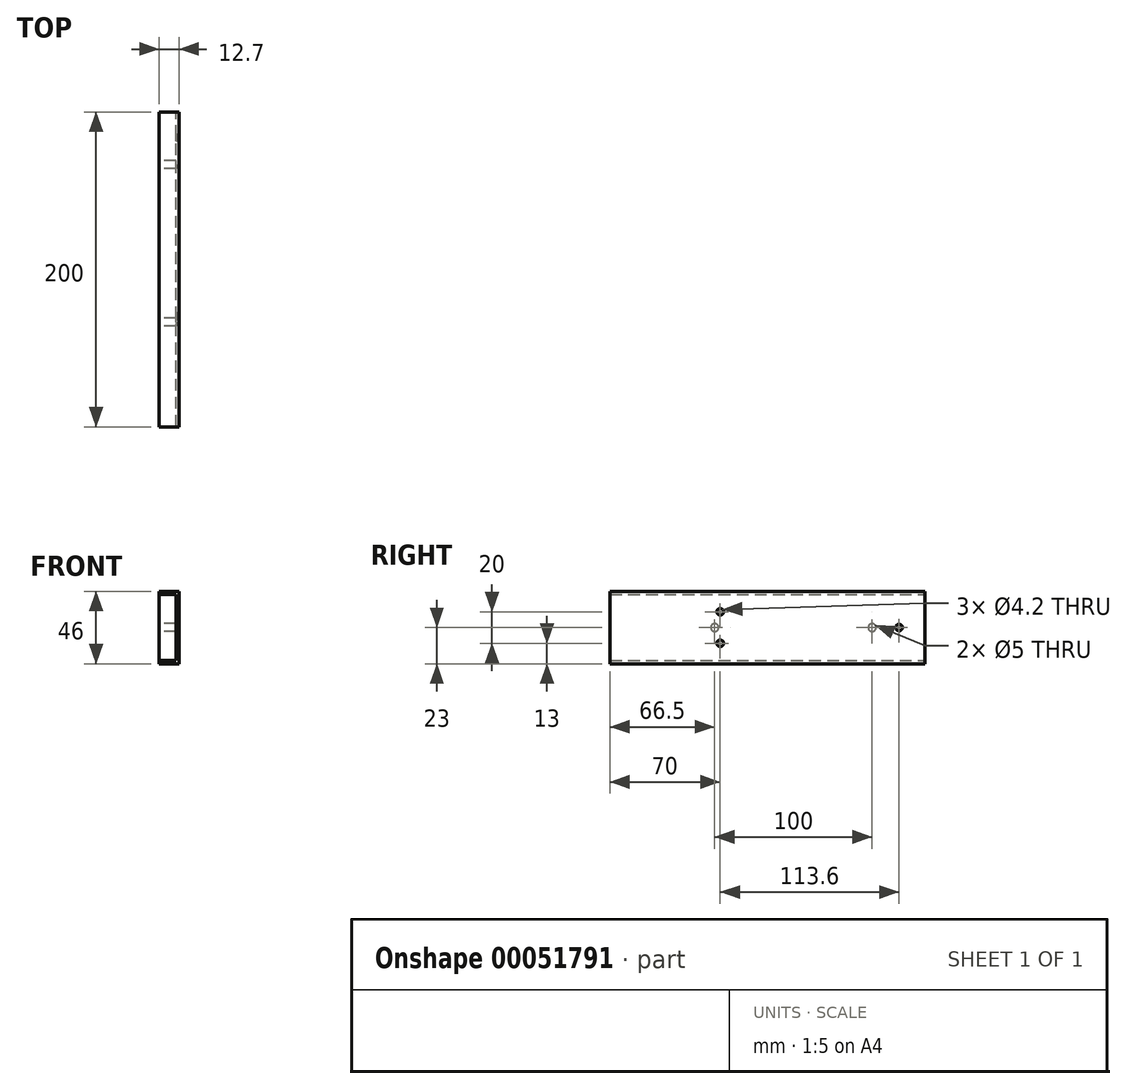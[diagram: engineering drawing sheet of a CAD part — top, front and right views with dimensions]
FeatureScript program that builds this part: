
annotation { "Feature Type Name" : "Feature", "Feature Type Description" : "" }
export const myFeature = defineFeature(function(context is Context, id is Id, definition is map)
    precondition{}
    {
        {
            var Q0;
            Q0=qCreatedBy(makeId("Front.planeOp"),FACE);
            var sketch = newSketch(context, id + "F3", { "sketchPlane" : qUnion([Q0])});
            skLineSegment(sketch, "E0.bottom", {"start": v(0, 0) * mm, "end": v(12.7, 0) * mm});
            skLineSegment(sketch, "E0.top", {"start": v(0, 46) * mm, "end": v(12.7, 46) * mm});
            skLineSegment(sketch, "E0.left", {"start": v(0, 0) * mm, "end": v(0, 2) * mm});
            skLineSegment(sketch, "E0.right", {"start": v(12.7, 0) * mm, "end": v(12.7, 46) * mm});
            skLineSegment(sketch, "E1.bottom", {"start": v(0, 44) * mm, "end": v(10.7, 44) * mm});
            skLineSegment(sketch, "E1.top", {"start": v(0, 2) * mm, "end": v(10.7, 2) * mm});
            skLineSegment(sketch, "E1.right", {"start": v(10.7, 44) * mm, "end": v(10.7, 2) * mm});
            skLineSegment(sketch, "E2.trimOffspring", {"start": v(0, 44) * mm, "end": v(0, 46) * mm});
            skSolve(sketch);
        }
        {
            var Q0;
            Q0=makeQuery(id+"F3.imprint","IMPRINT",FACE,{"disambiguationData":[TD([[makeQuery(id+"F3.imprint","IMPRINT",EDGE,{"derivedFrom":sQuery(id+"F3.wireOp",EDGE,"E0.bottom")}),1.0]])]});
            extrude(context, id + "F0", {"entities" : qUnion([Q0]), "depth" : 200 * mm});
        }
        {
            var Q0;
            Q0=makeQuery(id+"F0.opExtrude","SWEPT_FACE",FACE,{"disambiguationData":[OSD([sQuery(id+"F3.wireOp",EDGE,"E1.right")])]});
            var sketch = newSketch(context, id + "F4", { "sketchPlane" : qUnion([Q0])});
            skLineSegment(sketch, "E3", {"start": v(16.4, 23) * mm, "end": v(130, 23) * mm, "construction": true});
            skLineSegment(sketch, "E4", {"start": v(130, 33) * mm, "end": v(130, 13) * mm, "construction": true});
            skPoint(sketch, "E5", {"position": v(130, 33) * mm});
            skPoint(sketch, "E6", {"position": v(130, 13) * mm});
            skPoint(sketch, "E7", {"position": v(16.4, 23) * mm});
            skSolve(sketch);
        }
        {
            var Q0;
            Q0=sQuery(id+"F4.wireOp",VERTEX,"E6");
            var Q1;
            Q1=sQuery(id+"F4.wireOp",VERTEX,"E5");
            var Q2;
            Q2=sQuery(id+"F4.wireOp",VERTEX,"E7");
            var Q3;
            Q3=makeQuery(id+"F0.opExtrude","SWEPT_BODY",BODY,{"disambiguationData":[OSD([sQuery(id+"F3.wireOp",EDGE,"E0.bottom"),sQuery(id+"F3.wireOp",EDGE,"E0.top"),sQuery(id+"F3.wireOp",EDGE,"E0.left"),sQuery(id+"F3.wireOp",EDGE,"E0.right"),sQuery(id+"F3.wireOp",EDGE,"E1.bottom"),sQuery(id+"F3.wireOp",EDGE,"E1.top"),sQuery(id+"F3.wireOp",EDGE,"E1.right"),sQuery(id+"F3.wireOp",EDGE,"E2.trimOffspring")])]});
            hole(context, id + "F5", {"style" : HoleStyle.SIMPLE, "endStyle" : HoleEndStyle.THROUGH, "holeDiameter" : 4.2 * mm, "locations" : qUnion([Q0, Q1, Q2]), "scope" : qUnion([Q3]), "isTappedThrough" : true});
        }
        {
            var Q0;
            Q0=qCreatedBy(makeId("Front.planeOp"),FACE);
            var sketch = newSketch(context, id + "F6", { "sketchPlane" : qUnion([Q0])});
            skLineSegment(sketch, "E8.bottom", {"start": v(0, 44) * mm, "end": v(10.7, 44) * mm});
            skLineSegment(sketch, "E8.top", {"start": v(0, 2) * mm, "end": v(10.7, 2) * mm});
            skLineSegment(sketch, "E8.left", {"start": v(0, 44) * mm, "end": v(0, 2) * mm});
            skLineSegment(sketch, "E8.right", {"start": v(10.7, 44) * mm, "end": v(10.7, 2) * mm});
            skSolve(sketch);
        }
        {
            var Q0;
            Q0=makeQuery(id+"F6.imprint","IMPRINT",FACE,{"disambiguationData":[TD([[makeQuery(id+"F6.imprint","IMPRINT",EDGE,{"derivedFrom":sQuery(id+"F6.wireOp",EDGE,"E8.bottom")}),-1.0]])]});
            extrude(context, id + "F1", {"entities" : qUnion([Q0]), "depth" : 200 * mm});
        }
        {
            var Q0;
            Q0=makeQuery(id+"F1.opExtrude","SWEPT_FACE",FACE,{"disambiguationData":[OSD([sQuery(id+"F6.wireOp",EDGE,"E8.left")])]});
            var sketch = newSketch(context, id + "F7", { "sketchPlane" : qUnion([Q0])});
            skLineSegment(sketch, "E9", {"start": v(33.5, 23) * mm, "end": v(133.5, 23) * mm, "construction": true});
            skPoint(sketch, "E10", {"position": v(33.5, 23) * mm});
            skPoint(sketch, "E11", {"position": v(133.5, 23) * mm});
            skSolve(sketch);
        }
        {
            var Q0;
            Q0=sQuery(id+"F7.wireOp",VERTEX,"E11");
            var Q1;
            Q1=sQuery(id+"F7.wireOp",VERTEX,"E10");
            var Q2;
            Q2=makeQuery(id+"F1.opExtrude","SWEPT_BODY",BODY,{"disambiguationData":[OSD([sQuery(id+"F6.wireOp",EDGE,"E8.bottom"),sQuery(id+"F6.wireOp",EDGE,"E8.top"),sQuery(id+"F6.wireOp",EDGE,"E8.left"),sQuery(id+"F6.wireOp",EDGE,"E8.right")])]});
            hole(context, id + "F2", {"style" : HoleStyle.SIMPLE, "endStyle" : HoleEndStyle.THROUGH, "holeDiameter" : 5 * mm, "locations" : qUnion([Q0, Q1]), "scope" : qUnion([Q2]), "isTappedThrough" : true});
        }
    });
